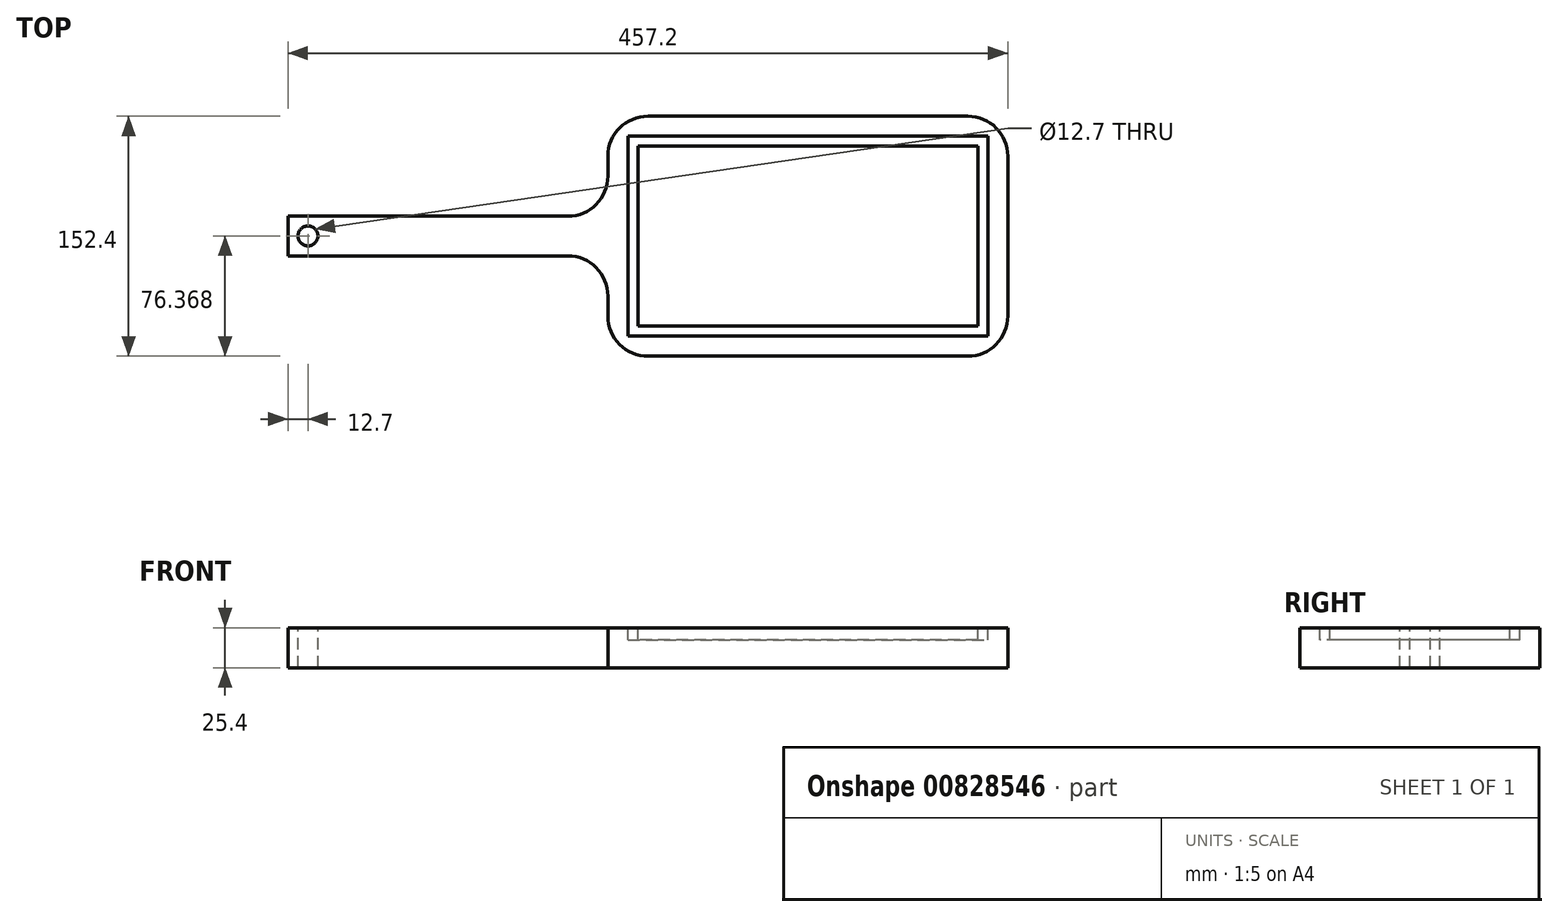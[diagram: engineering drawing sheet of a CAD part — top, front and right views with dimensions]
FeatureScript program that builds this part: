
annotation { "Feature Type Name" : "Feature", "Feature Type Description" : "" }
export const myFeature = defineFeature(function(context is Context, id is Id, definition is map)
    precondition{}
    {
        {
            var Q0;
            Q0=qCreatedBy(makeId("Top.planeOp"),FACE);
            var sketch = newSketch(context, id + "F0", { "sketchPlane" : qUnion([Q0])});
            skLineSegment(sketch, "E0.bottom", {"start": v(0, 0) * mm, "end": v(254, 0) * mm});
            skLineSegment(sketch, "E0.top", {"start": v(0, 152.4) * mm, "end": v(254, 152.4) * mm});
            skLineSegment(sketch, "E0.left", {"start": v(0, 0) * mm, "end": v(0, 152.4) * mm});
            skLineSegment(sketch, "E0.right", {"start": v(254, 0) * mm, "end": v(254, 152.4) * mm});
            skLineSegment(sketch, "E1.bottom", {"start": v(0, 88.9) * mm, "end": v(-203.2, 88.9) * mm});
            skLineSegment(sketch, "E1.top", {"start": v(0, 63.67) * mm, "end": v(-203.2, 63.67) * mm});
            skLineSegment(sketch, "E1.left", {"start": v(0, 88.9) * mm, "end": v(0, 63.67) * mm});
            skLineSegment(sketch, "E1.right", {"start": v(-203.2, 88.9) * mm, "end": v(-203.2, 63.67) * mm});
            skSolve(sketch);
        }
        {
            var Q0;
            Q0=makeQuery(id+"F0.imprint","IMPRINT",FACE,{"disambiguationData":[TD([[makeQuery(id+"F0.imprint","IMPRINT",EDGE,{"derivedFrom":sQuery(id+"F0.wireOp",EDGE,"E1.bottom")}),1.0]])]});
            var Q1;
            {var subQ3=sQuery(id+"F0.wireOp",EDGE,"E0.bottom");Q1=makeQuery(id+"F0.imprint","IMPRINT",FACE,{"disambiguationData":[TD([[makeQuery(id+"F0.imprint","IMPRINT",EDGE,{"derivedFrom":subQ3}),1.0]])]});}
            extrude(context, id + "F1", {"entities" : qUnion([Q0, Q1]), "oppositeDirection" : true, "depth" : 25.4 * mm, "offsetDistance" : 25.4 * mm});
        }
        {
            var Q0;
            Q0=makeQuery(id+"F1.opExtrude","CAP_FACE",FACE,{"disambiguationData":[OSD([sQuery(id+"F0.wireOp",EDGE,"E0.bottom"),sQuery(id+"F0.wireOp",EDGE,"E0.top"),sQuery(id+"F0.wireOp",EDGE,"E0.left"),sQuery(id+"F0.wireOp",EDGE,"E0.right"),sQuery(id+"F0.wireOp",EDGE,"E1.bottom"),sQuery(id+"F0.wireOp",EDGE,"E1.top"),sQuery(id+"F0.wireOp",EDGE,"E1.right")])],"isStart":true});
            var sketch = newSketch(context, id + "F2", { "sketchPlane" : qUnion([Q0])});
            skCircle(sketch, "E2", {"center": v(-190.5, 76.37) * mm, "radius": 6.35 * mm});
            skSolve(sketch);
        }
        {
            var Q0;
            Q0=makeQuery(id+"F2.imprint","IMPRINT",FACE,{"disambiguationData":[TD([[makeQuery(id+"F2.imprint","IMPRINT",EDGE,{"derivedFrom":sQuery(id+"F2.wireOp",EDGE,"E2")}),1.0]])]});
            extrude(context, id + "F3", {"entities" : qUnion([Q0]), "operationType" : NewBodyOperationType.REMOVE, "oppositeDirection" : true, "depth" : 25.4 * mm, "offsetDistance" : 25.4 * mm});
        }
        {
            var Q0;
            Q0=makeQuery(id+"F1.opExtrude","CAP_FACE",FACE,{"disambiguationData":[OSD([sQuery(id+"F0.wireOp",EDGE,"E0.bottom"),sQuery(id+"F0.wireOp",EDGE,"E0.top"),sQuery(id+"F0.wireOp",EDGE,"E0.left"),sQuery(id+"F0.wireOp",EDGE,"E0.right"),sQuery(id+"F0.wireOp",EDGE,"E1.bottom"),sQuery(id+"F0.wireOp",EDGE,"E1.top"),sQuery(id+"F0.wireOp",EDGE,"E1.right")])],"isStart":true});
            var sketch = newSketch(context, id + "F4", { "sketchPlane" : qUnion([Q0])});
            skLineSegment(sketch, "E3.3", {"start": v(19.05, 133.35) * mm, "end": v(19.05, 69.85) * mm});
            skLineSegment(sketch, "E3.4", {"start": v(19.05, 82.72) * mm, "end": v(19.05, 19.05) * mm});
            skLineSegment(sketch, "E3.5", {"start": v(19.05, 19.05) * mm, "end": v(234.95, 19.05) * mm});
            skLineSegment(sketch, "E3.6", {"start": v(234.95, 19.05) * mm, "end": v(234.95, 133.35) * mm});
            skLineSegment(sketch, "E3.7", {"start": v(234.95, 133.35) * mm, "end": v(19.05, 133.35) * mm});
            skLineSegment(sketch, "E4.3", {"start": v(6.35, 82.72) * mm, "end": v(6.35, 82.55) * mm});
            skLineSegment(sketch, "E5.0", {"start": v(-190.5, 76.37) * mm, "end": v(-190.5, 76.2) * mm});
            skLineSegment(sketch, "E5.3", {"start": v(12.7, 139.7) * mm, "end": v(12.7, 76.2) * mm});
            skLineSegment(sketch, "E5.4", {"start": v(12.7, 76.37) * mm, "end": v(12.7, 12.7) * mm});
            skLineSegment(sketch, "E5.5", {"start": v(12.7, 12.7) * mm, "end": v(241.3, 12.7) * mm});
            skLineSegment(sketch, "E5.6", {"start": v(241.3, 12.7) * mm, "end": v(241.3, 139.7) * mm});
            skLineSegment(sketch, "E5.7", {"start": v(241.3, 139.7) * mm, "end": v(12.7, 139.7) * mm});
            skSolve(sketch);
        }
        {
            var Q0;
            {var subQ4=sQuery(id+"F4.wireOp",EDGE,"E3.3");Q0=makeQuery(id+"F4.imprint","IMPRINT",FACE,{"disambiguationData":[TD([[makeQuery(id+"F4.imprint","IMPRINT",EDGE,{"derivedFrom":subQ4}),-1.0]])]});}
            extrude(context, id + "F5", {"entities" : qUnion([Q0]), "operationType" : NewBodyOperationType.REMOVE, "oppositeDirection" : true, "depth" : 7.62 * mm, "offsetDistance" : 25.4 * mm});
        }
        {
            var Q0;
            Q0=makeQuery(id+"F1.opExtrude","SWEPT_EDGE",EDGE,{"disambiguationData":[OSD([sQuery(id+"F0.wireOp",EDGE,"E0.top"),sQuery(id+"F0.wireOp",EDGE,"E0.left")])]});
            var Q1;
            Q1=makeQuery(id+"F1.opExtrude","SWEPT_EDGE",EDGE,{"disambiguationData":[OSD([sQuery(id+"F0.wireOp",EDGE,"E0.left"),sQuery(id+"F0.wireOp",EDGE,"E1.bottom"),sQuery(id+"F0.wireOp",EDGE,"E1.left")])]});
            fillet(context, id + "F6", {"entities" : qUnion([Q0, Q1]), "radius" : 25.4 * mm, "tangentPropagation" : true, "allowEdgeOverflow" : false});
        }
        {
            var Q0;
            Q0=makeQuery(id+"F1.opExtrude","SWEPT_EDGE",EDGE,{"disambiguationData":[OSD([sQuery(id+"F0.wireOp",EDGE,"E0.left"),sQuery(id+"F0.wireOp",EDGE,"E1.top"),sQuery(id+"F0.wireOp",EDGE,"E1.left")])]});
            var Q1;
            Q1=makeQuery(id+"F1.opExtrude","SWEPT_EDGE",EDGE,{"disambiguationData":[OSD([sQuery(id+"F0.wireOp",EDGE,"E0.bottom"),sQuery(id+"F0.wireOp",EDGE,"E0.left")])]});
            var Q2;
            Q2=makeQuery(id+"F1.opExtrude","SWEPT_EDGE",EDGE,{"disambiguationData":[OSD([sQuery(id+"F0.wireOp",EDGE,"E0.top"),sQuery(id+"F0.wireOp",EDGE,"E0.right")])]});
            var Q3;
            Q3=makeQuery(id+"F1.opExtrude","SWEPT_EDGE",EDGE,{"disambiguationData":[OSD([sQuery(id+"F0.wireOp",EDGE,"E0.bottom"),sQuery(id+"F0.wireOp",EDGE,"E0.right")])]});
            fillet(context, id + "F7", {"entities" : qUnion([Q0, Q1, Q2, Q3]), "radius" : 25.4 * mm, "tangentPropagation" : true, "allowEdgeOverflow" : false});
        }
    });
